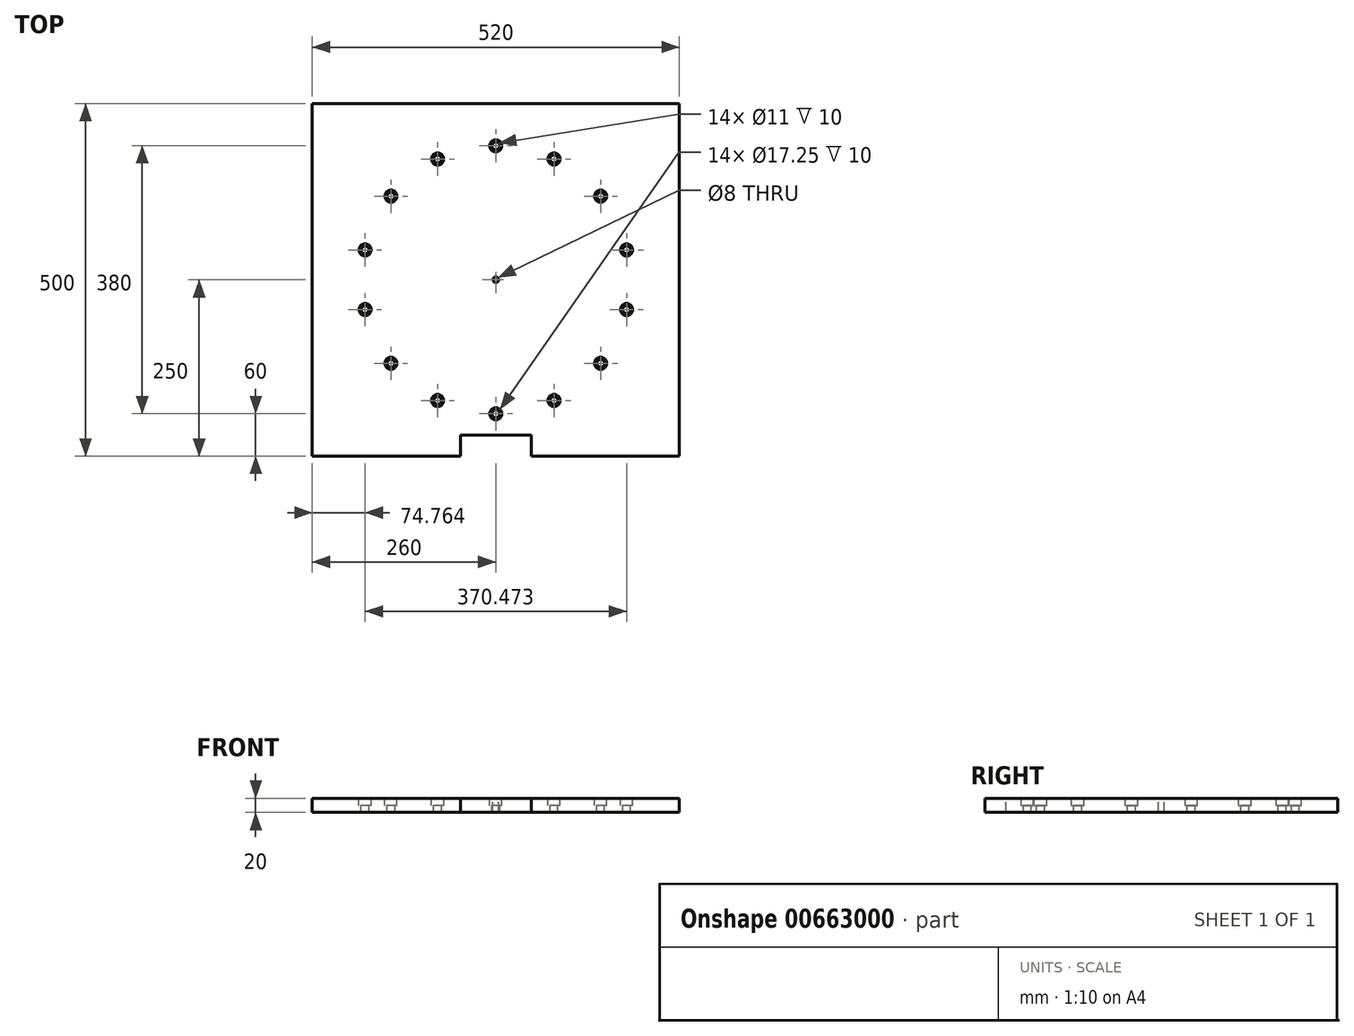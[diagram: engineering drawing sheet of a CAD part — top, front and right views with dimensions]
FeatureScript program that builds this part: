
annotation { "Feature Type Name" : "Feature", "Feature Type Description" : "" }
export const myFeature = defineFeature(function(context is Context, id is Id, definition is map)
    precondition{}
    {
        {
            var Q0;
            Q0=qCreatedBy(makeId("Top.planeOp"),FACE);
            var sketch = newSketch(context, id + "F0", { "sketchPlane" : qUnion([Q0])});
            skLineSegment(sketch, "E0.bottom", {"start": v(260, -250) * mm, "end": v(-260, -250) * mm});
            skLineSegment(sketch, "E0.top", {"start": v(260, 250) * mm, "end": v(-260, 250) * mm});
            skLineSegment(sketch, "E0.left", {"start": v(260, -250) * mm, "end": v(260, 250) * mm});
            skLineSegment(sketch, "E0.right", {"start": v(-260, -250) * mm, "end": v(-260, 250) * mm});
            skPoint(sketch, "E0.middle", {"position": v(0, 0) * mm});
            skSolve(sketch);
        }
        {
            var Q0;
            Q0=makeQuery(id+"F0.imprint","IMPRINT",FACE,{"disambiguationData":[TD([[makeQuery(id+"F0.imprint","IMPRINT",EDGE,{"derivedFrom":sQuery(id+"F0.wireOp",EDGE,"E0.bottom")}),-1.0]])]});
            extrude(context, id + "F1", {"entities" : qUnion([Q0]), "depth" : 20 * mm, "offsetDistance" : 25 * mm});
        }
        {
            var Q0;
            Q0=makeQuery(id+"F1.opExtrude","CAP_FACE",FACE,{"disambiguationData":[OSD([sQuery(id+"F0.wireOp",EDGE,"E0.bottom"),sQuery(id+"F0.wireOp",EDGE,"E0.top"),sQuery(id+"F0.wireOp",EDGE,"E0.left"),sQuery(id+"F0.wireOp",EDGE,"E0.right")])],"isStart":false});
            var sketch = newSketch(context, id + "F2", { "sketchPlane" : qUnion([Q0])});
            skCircle(sketch, "E1", {"center": v(0, 0) * mm, "radius": 190 * mm, "construction": true});
            skPoint(sketch, "E2", {"position": v(0, 190) * mm});
            skLineSegment(sketch, "E3", {"start": v(0, 190) * mm, "end": v(0, 0) * mm, "construction": true});
            skPoint(sketch, "E4.1.0", {"position": v(-82.44, 171.18) * mm});
            skPoint(sketch, "E4.2.0", {"position": v(-148.55, 118.46) * mm});
            skPoint(sketch, "E4.3.0", {"position": v(-185.24, 42.28) * mm});
            skPoint(sketch, "E4.4.0", {"position": v(-185.24, -42.28) * mm});
            skPoint(sketch, "E4.5.0", {"position": v(-148.55, -118.46) * mm});
            skPoint(sketch, "E4.6.0", {"position": v(-82.44, -171.18) * mm});
            skPoint(sketch, "E4.7.0", {"position": v(0, -190) * mm});
            skPoint(sketch, "E4.8.0", {"position": v(82.44, -171.18) * mm});
            skPoint(sketch, "E4.9.0", {"position": v(148.55, -118.46) * mm});
            skPoint(sketch, "E4.10.0", {"position": v(185.24, -42.28) * mm});
            skPoint(sketch, "E4.11.0", {"position": v(185.24, 42.28) * mm});
            skPoint(sketch, "E4.12.0", {"position": v(148.55, 118.46) * mm});
            skPoint(sketch, "E4.13.0", {"position": v(82.44, 171.18) * mm});
            skSolve(sketch);
        }
        {
            var Q0;
            Q0=sQuery(id+"F2.wireOp",VERTEX,"E2");
            var Q1;
            Q1=sQuery(id+"F2.wireOp",VERTEX,"E4.13.0");
            var Q2;
            Q2=sQuery(id+"F2.wireOp",VERTEX,"E4.12.0");
            var Q3;
            Q3=sQuery(id+"F2.wireOp",VERTEX,"E4.11.0");
            var Q4;
            Q4=sQuery(id+"F2.wireOp",VERTEX,"E4.10.0");
            var Q5;
            Q5=sQuery(id+"F2.wireOp",VERTEX,"E4.9.0");
            var Q6;
            Q6=sQuery(id+"F2.wireOp",VERTEX,"E4.8.0");
            var Q7;
            Q7=sQuery(id+"F2.wireOp",VERTEX,"E4.7.0");
            var Q8;
            Q8=sQuery(id+"F2.wireOp",VERTEX,"E4.6.0");
            var Q9;
            Q9=sQuery(id+"F2.wireOp",VERTEX,"E4.5.0");
            var Q10;
            Q10=sQuery(id+"F2.wireOp",VERTEX,"E4.4.0");
            var Q11;
            Q11=sQuery(id+"F2.wireOp",VERTEX,"E4.3.0");
            var Q12;
            Q12=sQuery(id+"F2.wireOp",VERTEX,"E4.2.0");
            var Q13;
            Q13=sQuery(id+"F2.wireOp",VERTEX,"E4.1.0");
            var Q14;
            Q14=makeQuery(id+"F1.opExtrude","SWEPT_BODY",BODY,{"disambiguationData":[OSD([sQuery(id+"F0.wireOp",EDGE,"E0.bottom"),sQuery(id+"F0.wireOp",EDGE,"E0.top"),sQuery(id+"F0.wireOp",EDGE,"E0.left"),sQuery(id+"F0.wireOp",EDGE,"E0.right")])]});
            hole(context, id + "F3", {"style" : HoleStyle.C_BORE, "endStyle" : HoleEndStyle.THROUGH, "standardTappedOrClearance" : lookupTablePath({ "fit" : "Normal", "standard" : "ISO", "size" : "M10", "type" : "Clearance" }), "standardBlindInLast" : lookupTablePath({ "fit" : "Normal", "standard" : "ISO", "engagement" : "75%", "pitch" : "1.5 mm", "size" : "M10", "type" : "Clearance & tapped" }), "holeDiameter" : 11 * mm, "cBoreDiameter" : 17.25 * mm, "cBoreDepth" : 10 * mm, "majorDiameter" : 5 * mm, "isTappedThrough" : true, "tappedDepth" : 12 * mm, "tapClearance" : 3, "locations" : qUnion([Q0, Q1, Q2, Q3, Q4, Q5, Q6, Q7, Q8, Q9, Q10, Q11, Q12, Q13]), "scope" : qUnion([Q14])});
        }
        {
            var Q0;
            Q0=sQuery(id+"F2.wireOp",VERTEX,"E1.center");
            var Q1;
            Q1=makeQuery(id+"F1.opExtrude","SWEPT_BODY",BODY,{"disambiguationData":[OSD([sQuery(id+"F0.wireOp",EDGE,"E0.bottom"),sQuery(id+"F0.wireOp",EDGE,"E0.top"),sQuery(id+"F0.wireOp",EDGE,"E0.left"),sQuery(id+"F0.wireOp",EDGE,"E0.right")])]});
            hole(context, id + "F4", {"style" : HoleStyle.SIMPLE, "endStyle" : HoleEndStyle.THROUGH, "standardTappedOrClearance" : lookupTablePath({ "standard" : "ISO", "size" : "8", "type" : "Drilled" }), "standardBlindInLast" : lookupTablePath({ "standard" : "ISO", "size" : "8", "type" : "Drilled" }), "holeDiameter" : 8 * mm, "majorDiameter" : 5 * mm, "isTappedThrough" : true, "tappedDepth" : 12 * mm, "tapClearance" : 3, "locations" : qUnion([Q0]), "scope" : qUnion([Q1])});
        }
        {
            var Q0;
            Q0=makeQuery(id+"F2.imprint","IMPRINT",FACE,{"disambiguationData":[TD([[makeQuery(id+"F2.imprint","IMPRINT",EDGE,{"derivedFrom":makeQuery(id+"F1.opExtrude","CAP_EDGE",EDGE,{"disambiguationData":[OSD([sQuery(id+"F0.wireOp",EDGE,"E0.bottom")])],"isStart":false})}),-1.0]])]});
            var sketch = newSketch(context, id + "F5", { "sketchPlane" : qUnion([Q0])});
            skLineSegment(sketch, "E5.bottom", {"start": v(-50, -250) * mm, "end": v(50, -250) * mm});
            skLineSegment(sketch, "E5.top", {"start": v(-50, -220) * mm, "end": v(50, -220) * mm});
            skLineSegment(sketch, "E5.left", {"start": v(-50, -250) * mm, "end": v(-50, -220) * mm});
            skLineSegment(sketch, "E5.right", {"start": v(50, -250) * mm, "end": v(50, -220) * mm});
            skSolve(sketch);
        }
        {
            var Q0;
            Q0=makeQuery(id+"F5.imprint","IMPRINT",FACE,{"disambiguationData":[TD([[makeQuery(id+"F5.imprint","IMPRINT",EDGE,{"derivedFrom":sQuery(id+"F5.wireOp",EDGE,"E5.bottom")}),-1.0]])]});
            extrude(context, id + "F6", {"entities" : qUnion([Q0]), "operationType" : NewBodyOperationType.REMOVE, "endBound" : BoundingType.THROUGH_ALL, "oppositeDirection" : true, "depth" : 25 * mm, "offsetDistance" : 25 * mm});
        }
    });
